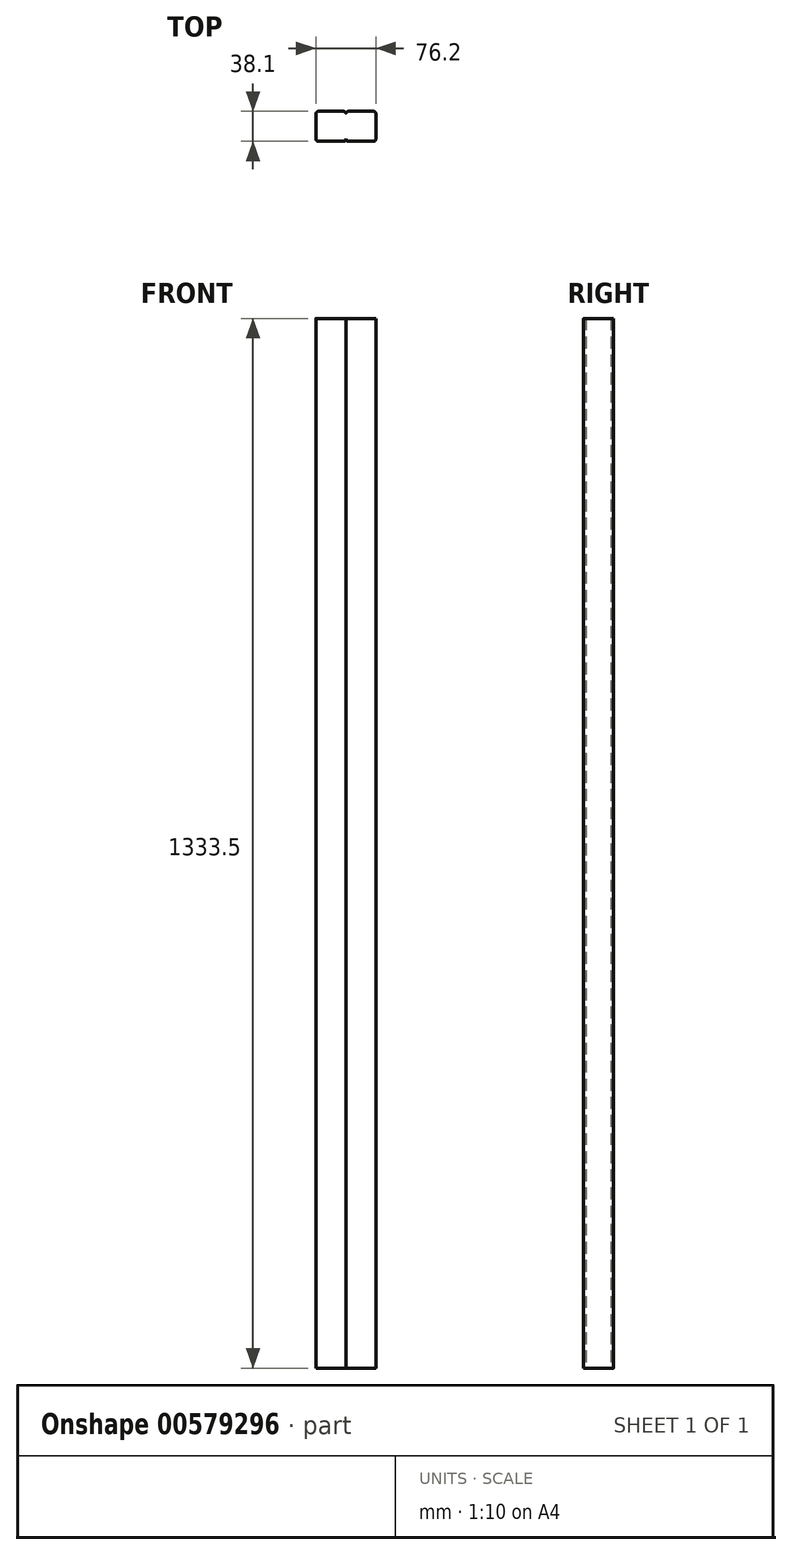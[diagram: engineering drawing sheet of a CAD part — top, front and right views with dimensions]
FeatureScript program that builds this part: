
annotation { "Feature Type Name" : "Feature", "Feature Type Description" : "" }
export const myFeature = defineFeature(function(context is Context, id is Id, definition is map)
    precondition{}
    {
        {
            var Q0;
            Q0=qCreatedBy(makeId("Top.planeOp"),FACE);
            var sketch = newSketch(context, id + "F0", { "sketchPlane" : qUnion([Q0])});
            skLineSegment(sketch, "E0.bottom", {"start": v(34.93, 19.05) * mm, "end": v(3.18, 19.05) * mm});
            skLineSegment(sketch, "E0.top", {"start": v(34.93, -19.05) * mm, "end": v(3.18, -19.05) * mm});
            skLineSegment(sketch, "E0.left", {"start": v(38.1, 15.88) * mm, "end": v(38.1, -15.87) * mm});
            skLineSegment(sketch, "E0.right", {"start": v(-38.1, 15.88) * mm, "end": v(-38.1, -15.88) * mm});
            skPoint(sketch, "E0.middle", {"position": v(0, 0) * mm});
            skLineSegment(sketch, "E1", {"start": v(0, 15.88) * mm, "end": v(0, -15.88) * mm});
            skPoint(sketch, "E2.newPointA", {"position": v(0, 19.05) * mm});
            skPoint(sketch, "E2.newPointB", {"position": v(-38.1, 19.05) * mm});
            skArc(sketch, "E2.filletArc", {"start": v(3.18, 19.05) * mm, "mid": v(0.93, 18.12) * mm, "end": v(0, 15.88) * mm});
            skPoint(sketch, "E3.visualSharp", {"position": v(38.1, 19.05) * mm});
            skArc(sketch, "E3.filletArc", {"start": v(38.1, 15.88) * mm, "mid": v(37.17, 18.12) * mm, "end": v(34.93, 19.05) * mm});
            skPoint(sketch, "E4.visualSharp", {"position": v(38.1, -19.05) * mm});
            skArc(sketch, "E4.filletArc", {"start": v(34.93, -19.05) * mm, "mid": v(37.17, -18.12) * mm, "end": v(38.1, -15.87) * mm});
            skPoint(sketch, "E5.newPointA", {"position": v(-38.1, -19.05) * mm});
            skPoint(sketch, "E5.newPointB", {"position": v(0, -19.05) * mm});
            skArc(sketch, "E5.filletArc", {"start": v(0, -15.88) * mm, "mid": v(0.93, -18.12) * mm, "end": v(3.17, -19.05) * mm});
            skLineSegment(sketch, "E6.bottom", {"start": v(-34.93, 19.05) * mm, "end": v(-3.18, 19.05) * mm});
            skLineSegment(sketch, "E6.top", {"start": v(-34.93, -19.05) * mm, "end": v(-3.18, -19.05) * mm});
            skArc(sketch, "E7.filletArc", {"start": v(-34.93, 19.05) * mm, "mid": v(-37.17, 18.12) * mm, "end": v(-38.1, 15.88) * mm});
            skArc(sketch, "E8.filletArc", {"start": v(0, 15.88) * mm, "mid": v(-0.93, 18.12) * mm, "end": v(-3.18, 19.05) * mm});
            skArc(sketch, "E9.filletArc", {"start": v(-3.18, -19.05) * mm, "mid": v(-0.93, -18.12) * mm, "end": v(0, -15.88) * mm});
            skArc(sketch, "E10.filletArc", {"start": v(-38.1, -15.88) * mm, "mid": v(-37.17, -18.12) * mm, "end": v(-34.93, -19.05) * mm});
            skSolve(sketch);
        }
        {
            var Q0;
            Q0 = qSketchRegion(id + "F0", true);
            extrude(context, id + "F1", {"entities" : qUnion([Q0]), "depth" : 1333.5 * mm, "offsetDistance" : 25.4 * mm});
        }
    });
